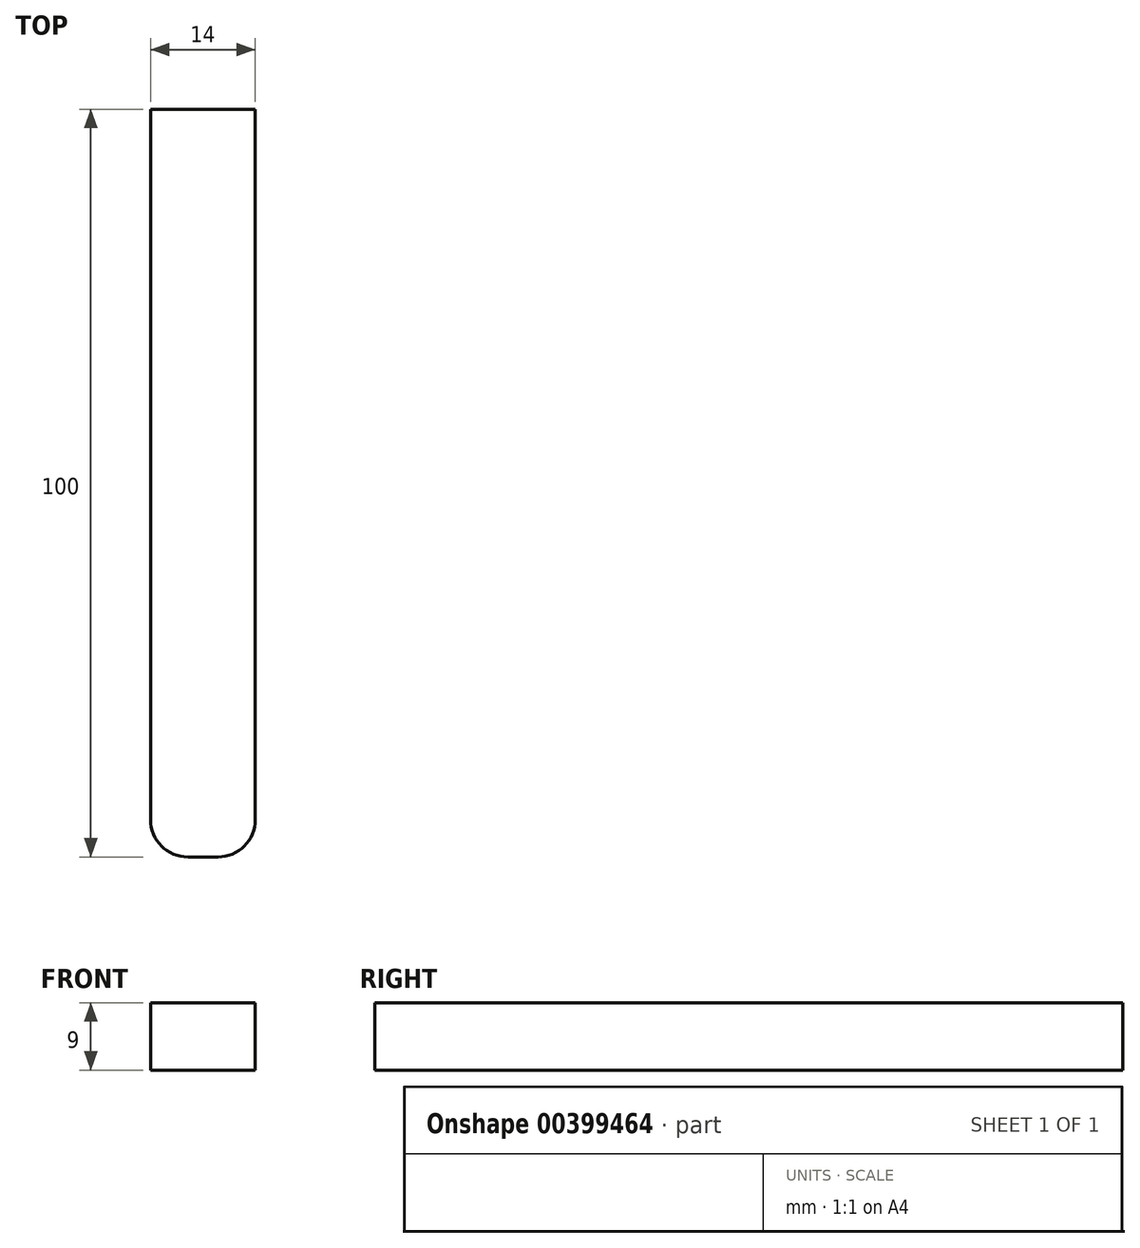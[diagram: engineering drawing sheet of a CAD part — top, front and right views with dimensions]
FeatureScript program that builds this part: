
annotation { "Feature Type Name" : "Feature", "Feature Type Description" : "" }
export const myFeature = defineFeature(function(context is Context, id is Id, definition is map)
    precondition{}
    {
        {
            var Q0;
            Q0=qCreatedBy(makeId("Front.planeOp"),FACE);
            var sketch = newSketch(context, id + "F0", { "sketchPlane" : qUnion([Q0])});
            skLineSegment(sketch, "E0.bottom", {"start": v(7, 4.5) * mm, "end": v(-7, 4.5) * mm});
            skLineSegment(sketch, "E0.top", {"start": v(7, -4.5) * mm, "end": v(-7, -4.5) * mm});
            skLineSegment(sketch, "E0.left", {"start": v(7, 4.5) * mm, "end": v(7, -4.5) * mm});
            skLineSegment(sketch, "E0.right", {"start": v(-7, 4.5) * mm, "end": v(-7, -4.5) * mm});
            skPoint(sketch, "E0.middle", {"position": v(0, 0) * mm});
            skSolve(sketch);
        }
        {
            var Q0;
            Q0 = qSketchRegion(id + "F0", true);
            extrude(context, id + "F1", {"entities" : qUnion([Q0]), "oppositeDirection" : true, "depth" : 100 * mm});
        }
        {
            var Q0;
            Q0=makeQuery(id+"F1.opExtrude","CAP_EDGE",EDGE,{"disambiguationData":[OSD([sQuery(id+"F0.wireOp",EDGE,"E0.right")])],"isStart":true});
            var Q1;
            Q1=makeQuery(id+"F1.opExtrude","CAP_EDGE",EDGE,{"disambiguationData":[OSD([sQuery(id+"F0.wireOp",EDGE,"E0.left")])],"isStart":true});
            fillet(context, id + "F2", {"entities" : qUnion([Q0, Q1]), "radius" : 5 * mm, "tangentPropagation" : true, "allowEdgeOverflow" : false});
        }
    });
